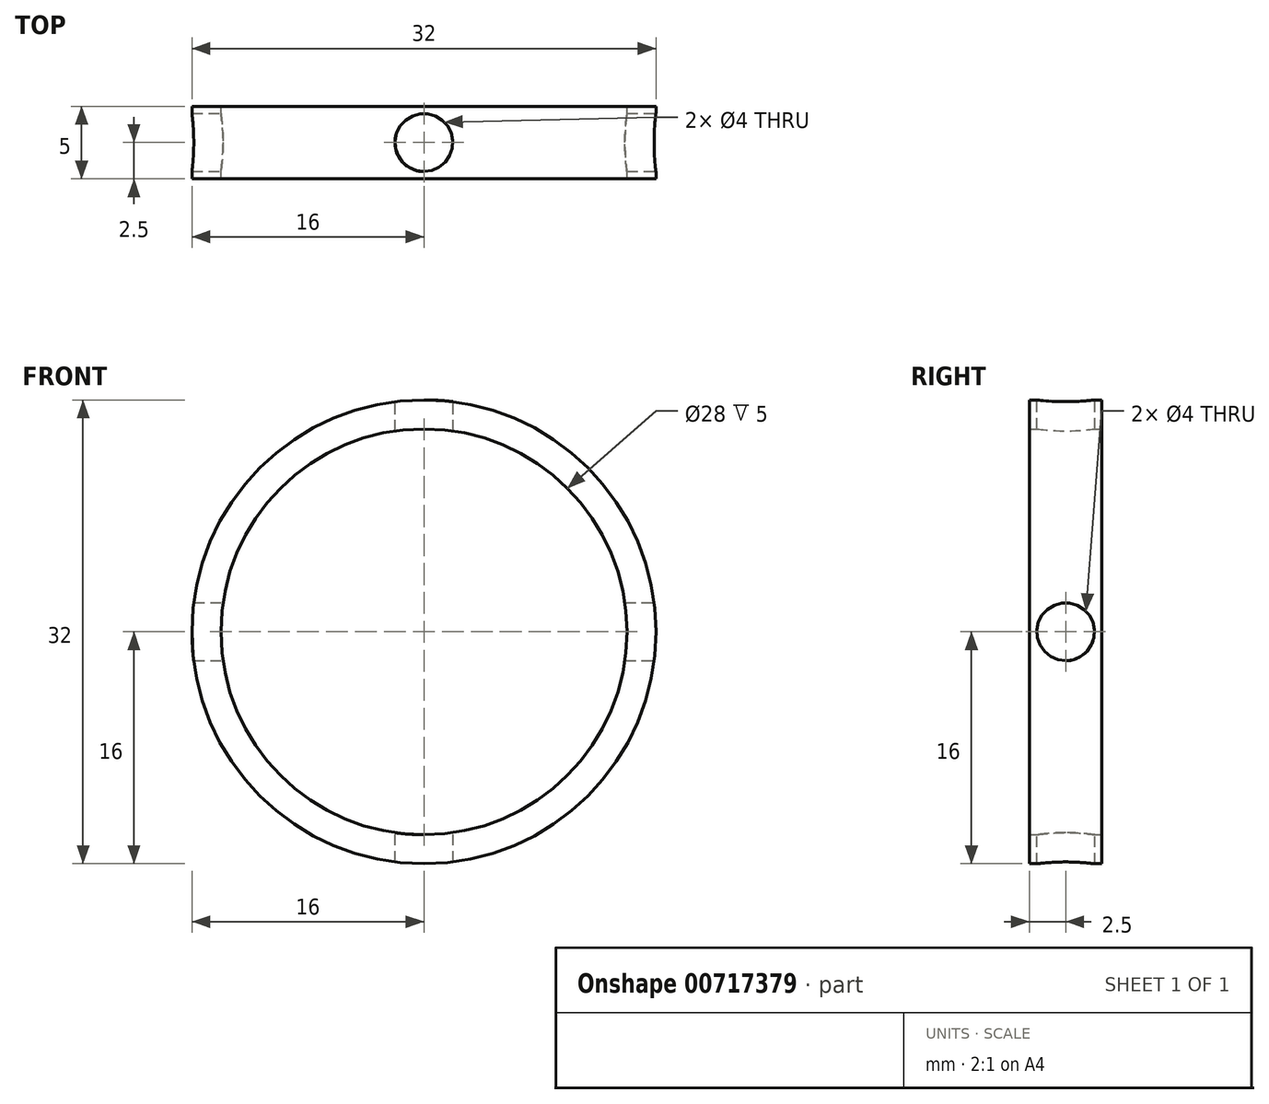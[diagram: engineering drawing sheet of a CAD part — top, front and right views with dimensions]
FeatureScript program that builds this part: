
annotation { "Feature Type Name" : "Feature", "Feature Type Description" : "" }
export const myFeature = defineFeature(function(context is Context, id is Id, definition is map)
    precondition{}
    {
        {
            var Q0;
            Q0=qCreatedBy(makeId("Front.planeOp"),FACE);
            var sketch = newSketch(context, id + "F0", { "sketchPlane" : qUnion([Q0])});
            skCircle(sketch, "E0", {"center": v(0, 0) * mm, "radius": 16 * mm});
            skCircle(sketch, "E1.0", {"center": v(0, 0) * mm, "radius": 14 * mm});
            skSolve(sketch);
        }
        {
            var Q0;
            Q0=makeQuery(id+"F0.imprint","IMPRINT",FACE,{"disambiguationData":[TD([[makeQuery(id+"F0.imprint","IMPRINT",EDGE,{"derivedFrom":sQuery(id+"F0.wireOp",EDGE,"E0")}),1.0]])]});
            extrude(context, id + "F1", {"entities" : qUnion([Q0]), "depth" : 5 * mm, "offsetDistance" : 25 * mm});
        }
        {
            var Q0;
            Q0=qCreatedBy(makeId("Right.planeOp"),FACE);
            cPlane(context, id + "F2", {"entities" : qUnion([Q0]), "cplaneType" : CPlaneType.OFFSET, "offset" : 16 * mm, "width" : 150 * mm, "height" : 150 * mm});
        }
        {
            var Q0;
            Q0=qCreatedBy(id+"F2.planeOp",FACE);
            var sketch = newSketch(context, id + "F3", { "sketchPlane" : qUnion([Q0])});
            skPoint(sketch, "E2", {"position": v(-2.5, 0) * mm});
            skSolve(sketch);
        }
        {
            var Q0;
            Q0=sQuery(id+"F3.wireOp",VERTEX,"E2");
            var Q1;
            Q1=makeQuery(id+"F1.opExtrude","SWEPT_BODY",BODY,{"disambiguationData":[OSD([sQuery(id+"F0.wireOp",EDGE,"E0"),sQuery(id+"F0.wireOp",EDGE,"E1.0")])]});
            hole(context, id + "F4", {"style" : HoleStyle.SIMPLE, "endStyle" : HoleEndStyle.THROUGH, "holeDiameter" : 4 * mm, "majorDiameter" : 5 * mm, "isTappedThrough" : true, "tappedDepth" : 12 * mm, "tapClearance" : 3, "locations" : qUnion([Q0]), "scope" : qUnion([Q1])});
        }
        {
            var Q0;
            Q0=qCreatedBy(makeId("Top.planeOp"),FACE);
            cPlane(context, id + "F5", {"entities" : qUnion([Q0]), "cplaneType" : CPlaneType.OFFSET, "offset" : 16 * mm, "width" : 150 * mm, "height" : 150 * mm});
        }
        {
            var Q0;
            Q0=qCreatedBy(id+"F5.planeOp",FACE);
            var sketch = newSketch(context, id + "F6", { "sketchPlane" : qUnion([Q0])});
            skPoint(sketch, "E3", {"position": v(0, -2.5) * mm});
            skSolve(sketch);
        }
        {
            var Q0;
            Q0=sQuery(id+"F6.wireOp",VERTEX,"E3");
            var Q1;
            Q1=makeQuery(id+"F1.opExtrude","SWEPT_BODY",BODY,{"disambiguationData":[OSD([sQuery(id+"F0.wireOp",EDGE,"E0"),sQuery(id+"F0.wireOp",EDGE,"E1.0")])]});
            hole(context, id + "F7", {"style" : HoleStyle.SIMPLE, "endStyle" : HoleEndStyle.THROUGH, "holeDiameter" : 4 * mm, "majorDiameter" : 5 * mm, "isTappedThrough" : true, "tappedDepth" : 12 * mm, "tapClearance" : 3, "locations" : qUnion([Q0]), "scope" : qUnion([Q1])});
        }
    });
